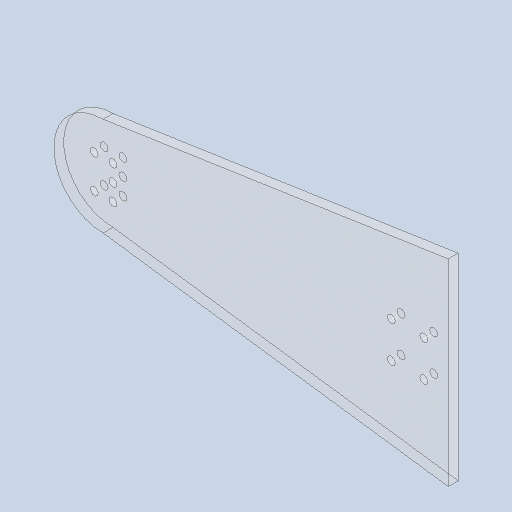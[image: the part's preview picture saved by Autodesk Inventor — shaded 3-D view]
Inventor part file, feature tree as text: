
AUTODESK INVENTOR PART (.ipt)
format: ipt  version: 2023.1 (Build 271208000, 208)  size: 170,496 bytes
history: native  units: in
note: dims shown in document units (in); Inventor stores cm internally (conversion verified against a paired STEP export)
features: reference x10, other x4, extrude x1
ambient origin geometry x8: Origin, YZ Plane, XZ Plane, XY Plane, X Axis, Y Axis, Z Axis, Center Point
bodies: Solid1 (feature_tree)
feature tree (15):
  extrude  "Extrusion1"  Depth=3.937in
  reference  "Reference2"
  reference  "Reference3"
  reference  "Reference4"
  reference  "Reference5"
  reference  "Reference6"
  reference  "Reference7"
  reference  "Reference8"
  reference  "Reference9"
  reference  "Reference10"
  reference  "Reference11"
  other  "Ensamble.iam"
  other  "base:1"
  other  "SoporteEncoder:1"
  other  "SoporteUnion:1"
